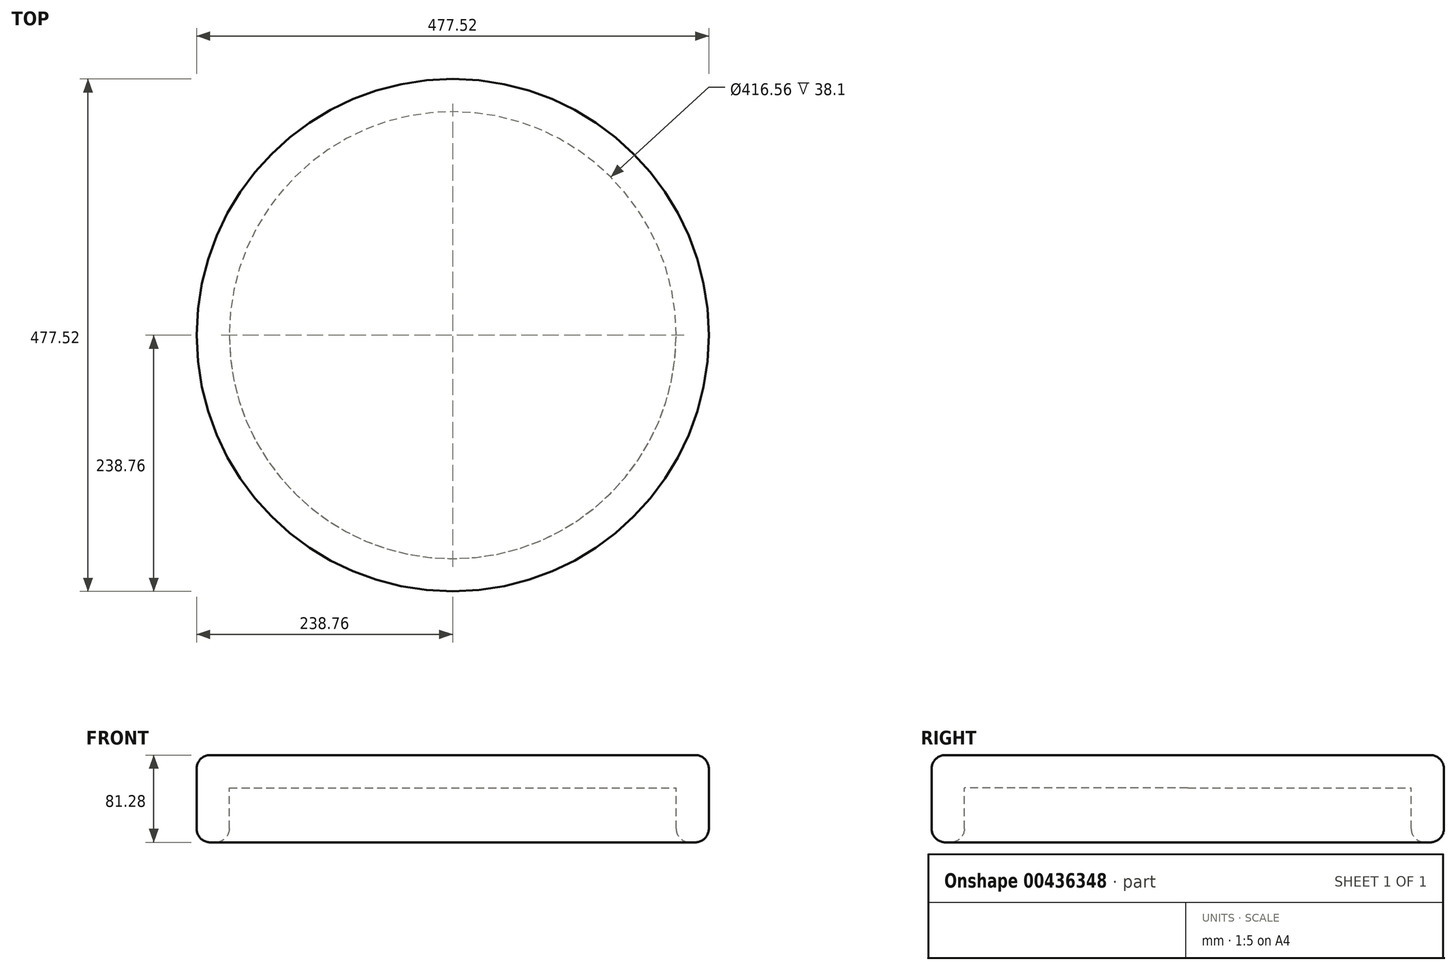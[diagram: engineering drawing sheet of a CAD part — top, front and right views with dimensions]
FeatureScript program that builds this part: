
annotation { "Feature Type Name" : "Feature", "Feature Type Description" : "" }
export const myFeature = defineFeature(function(context is Context, id is Id, definition is map)
    precondition{}
    {
        {
            var Q0;
            Q0=qCreatedBy(makeId("Front.planeOp"),FACE);
            var sketch = newSketch(context, id + "F0", { "sketchPlane" : qUnion([Q0])});
            skLineSegment(sketch, "E0", {"start": v(0, 0) * mm, "end": v(-238.76, 0) * mm});
            skLineSegment(sketch, "E1", {"start": v(-238.76, 0) * mm, "end": v(-238.76, 81.28) * mm});
            skLineSegment(sketch, "E2", {"start": v(-238.76, 81.28) * mm, "end": v(0, 81.28) * mm});
            skLineSegment(sketch, "E3", {"start": v(0, 81.28) * mm, "end": v(0, 0) * mm});
            skSolve(sketch);
        }
        {
            var Q0;
            Q0=makeQuery(id+"F0.imprint","IMPRINT",FACE,{"disambiguationData":[TD([[makeQuery(id+"F0.imprint","IMPRINT",EDGE,{"derivedFrom":sQuery(id+"F0.wireOp",EDGE,"E0")}),-1.0]])]});
            var Q1;
            Q1=sQuery(id+"F0.wireOp",EDGE,"E3");
            revolve(context, id + "F1", {"entities" : qUnion([Q0]), "axis" : qUnion([Q1]), "revolveType" : RevolveType.FULL});
        }
        {
            var Q0;
            Q0=makeQuery(id+"F1.opRevolve","SWEPT_FACE",FACE,{"disambiguationData":[OSD([sQuery(id+"F0.wireOp",EDGE,"E0")])]});
            shell(context, id + "F2", {"entities" : qUnion([Q0]), "thickness" : 30.48 * mm});
        }
        {
            var Q0;
            Q0=makeQuery(id+"F1.opRevolve","SWEPT_FACE",FACE,{"disambiguationData":[OSD([sQuery(id+"F0.wireOp",EDGE,"E2")])]});
            var Q1;
            Q1=makeQuery(id+"F1.opRevolve","SWEPT_FACE",FACE,{"disambiguationData":[OSD([sQuery(id+"F0.wireOp",EDGE,"E0")])]});
            fillet(context, id + "F3", {"entities" : qUnion([Q0, Q1]), "radius" : 12.7 * mm, "tangentPropagation" : true, "allowEdgeOverflow" : false});
        }
    });
